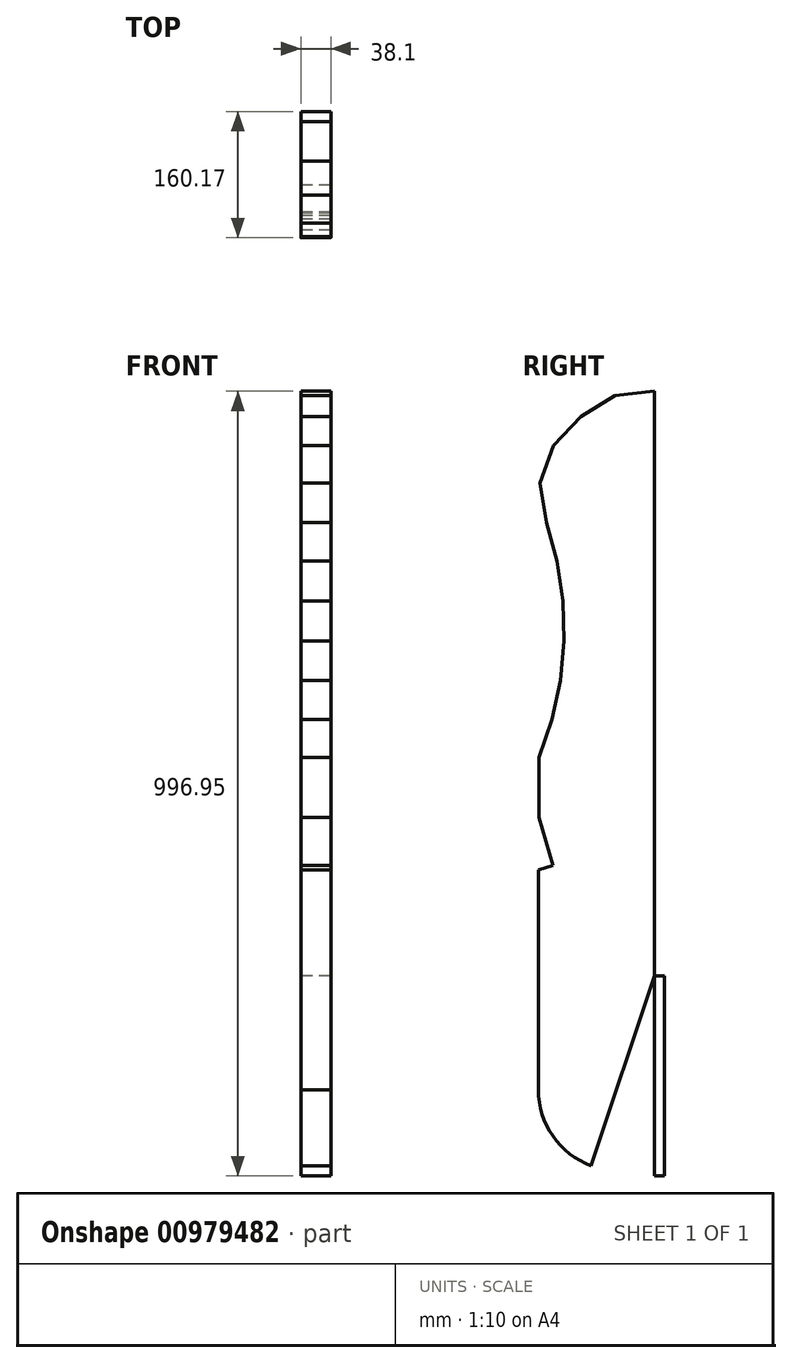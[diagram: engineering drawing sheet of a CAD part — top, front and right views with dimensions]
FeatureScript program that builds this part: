
annotation { "Feature Type Name" : "Feature", "Feature Type Description" : "" }
export const myFeature = defineFeature(function(context is Context, id is Id, definition is map)
    precondition{}
    {
        {
            var Q0;
            Q0=qCreatedBy(makeId("Right.planeOp"),FACE);
            var sketch = newSketch(context, id + "F0", { "sketchPlane" : qUnion([Q0])});
            skLineSegment(sketch, "E0", {"start": v(-143.71, 464.44) * mm, "end": v(-186.68, 437.35) * mm});
            skLineSegment(sketch, "E1", {"start": v(-186.68, 437.35) * mm, "end": v(-221.85, 400.7) * mm});
            skLineSegment(sketch, "E2", {"start": v(-221.85, 400.7) * mm, "end": v(-239, 352.87) * mm});
            skLineSegment(sketch, "E3", {"start": v(-239, 352.87) * mm, "end": v(-230.77, 302.74) * mm});
            skLineSegment(sketch, "E4", {"start": v(-143.71, 464.44) * mm, "end": v(-93.2, 469.82) * mm});
            skLineSegment(sketch, "E5", {"start": v(-93.2, 469.82) * mm, "end": v(-93.2, -273.13) * mm});
            skLineSegment(sketch, "E6", {"start": v(-240.66, -138.04) * mm, "end": v(-222.35, -132.78) * mm});
            skLineSegment(sketch, "E7", {"start": v(-222.35, -132.78) * mm, "end": v(-239.9, -71.75) * mm});
            skLineSegment(sketch, "E8", {"start": v(-239.9, -71.75) * mm, "end": v(-239.9, 4.45) * mm});
            skLineSegment(sketch, "E9", {"start": v(-240.66, -138.04) * mm, "end": v(-240.66, -417.44) * mm});
            skArc(sketch, "E10", {"start": v(-240.04, -407.27) * mm, "mid": v(-225.4, -472.1) * mm, "end": v(-173.8, -514) * mm});
            skArc(sketch, "E11", {"start": v(-239.9, 4.45) * mm, "mid": v(-208.18, 152.76) * mm, "end": v(-230.77, 302.74) * mm});
            skLineSegment(sketch, "E12", {"start": v(-173.8, -514) * mm, "end": v(-93.2, -273.13) * mm});
            skLineSegment(sketch, "E13", {"start": v(-230.77, 302.74) * mm, "end": v(-217.24, 253.77) * mm});
            skLineSegment(sketch, "E14", {"start": v(-217.24, 253.77) * mm, "end": v(-209.67, 203.54) * mm});
            skLineSegment(sketch, "E15", {"start": v(-209.67, 203.54) * mm, "end": v(-208.18, 152.76) * mm});
            skLineSegment(sketch, "E16", {"start": v(-208.18, 152.76) * mm, "end": v(-212.77, 102.17) * mm});
            skLineSegment(sketch, "E17", {"start": v(-212.77, 102.17) * mm, "end": v(-223.4, 52.5) * mm});
            skLineSegment(sketch, "E18", {"start": v(-223.4, 52.5) * mm, "end": v(-239.9, 4.45) * mm});
            skLineSegment(sketch, "E19", {"start": v(-93.2, -273.13) * mm, "end": v(-93.2, -527.13) * mm});
            skLineSegment(sketch, "E20.bottom", {"start": v(-93.2, -527.13) * mm, "end": v(-80.5, -527.13) * mm});
            skLineSegment(sketch, "E20.top", {"start": v(-93.2, -273.13) * mm, "end": v(-80.5, -273.13) * mm});
            skLineSegment(sketch, "E20.left", {"start": v(-93.2, -527.13) * mm, "end": v(-93.2, -273.13) * mm});
            skLineSegment(sketch, "E20.right", {"start": v(-80.5, -527.13) * mm, "end": v(-80.5, -273.13) * mm});
            skSolve(sketch);
        }
        {
            var Q0;
            Q0=qSketchRegion(id+"F0",true);
            extrude(context, id + "F1", {"entities" : qUnion([Q0]), "depth" : 38.1 * mm});
        }
        {
            var Q0;
            Q0=makeQuery(id+"F0.imprint","IMPRINT",FACE,{"disambiguationData":[TD([[makeQuery(id+"F0.imprint","IMPRINT",EDGE,{"derivedFrom":sQuery(id+"F0.wireOp",EDGE,"E20.bottom")}),1.0]])]});
            extrude(context, id + "F2", {"entities" : qUnion([Q0]), "operationType" : NewBodyOperationType.ADD, "depth" : 25.4 * mm});
        }
    });
